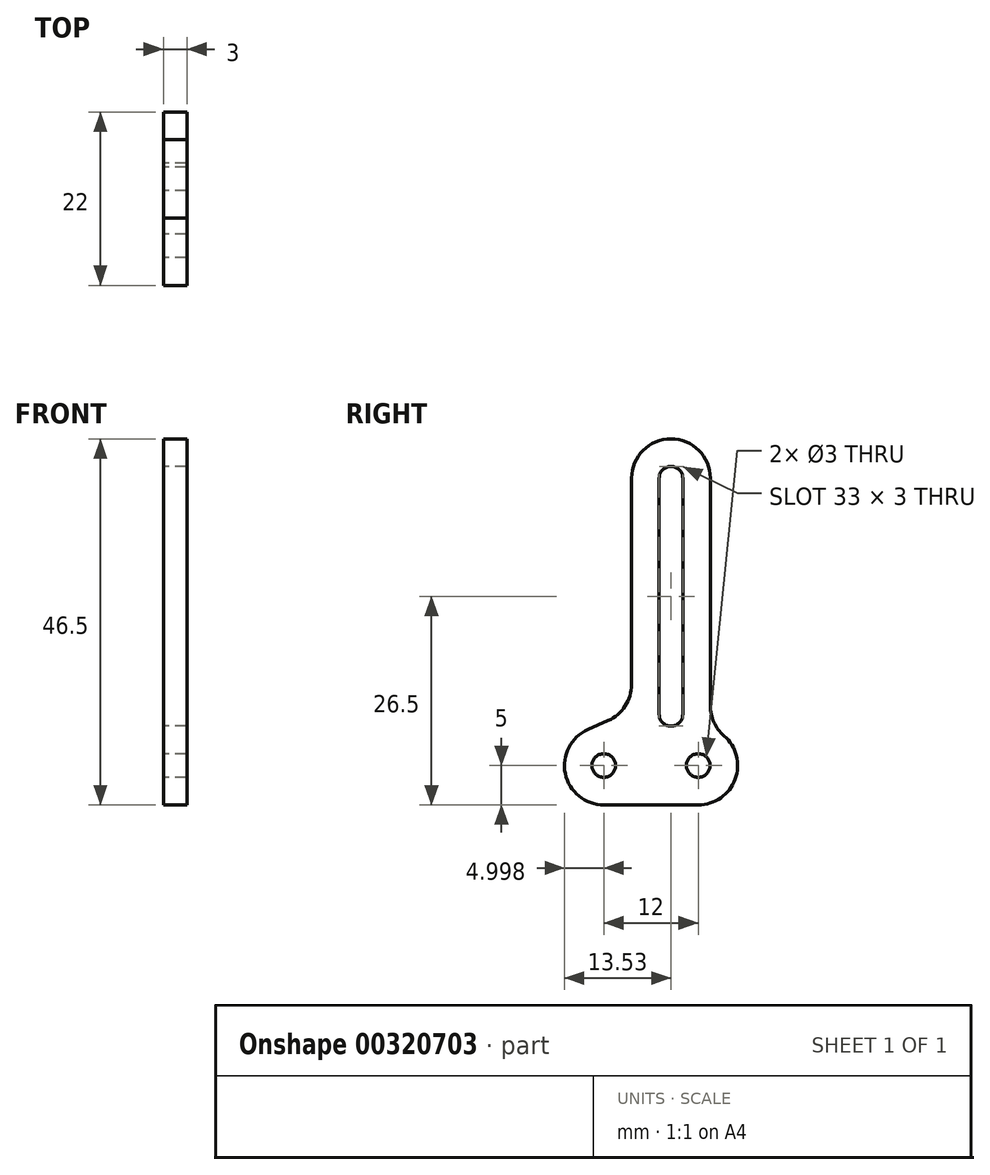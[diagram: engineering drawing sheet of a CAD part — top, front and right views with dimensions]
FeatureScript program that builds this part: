
annotation { "Feature Type Name" : "Feature", "Feature Type Description" : "" }
export const myFeature = defineFeature(function(context is Context, id is Id, definition is map)
    precondition{}
    {
        {
            var Q0;
            Q0=qCreatedBy(makeId("Right.planeOp"),FACE);
            var sketch = newSketch(context, id + "F0", { "sketchPlane" : qUnion([Q0])});
            skCircle(sketch, "E0", {"center": v(-8.53, 0) * mm, "radius": 1.5 * mm});
            skCircle(sketch, "E1", {"center": v(3.47, 0) * mm, "radius": 1.5 * mm});
            skArc(sketch, "E2", {"start": v(5, 36.5) * mm, "mid": v(0, 41.5) * mm, "end": v(-5, 36.5) * mm});
            skArc(sketch, "E3", {"start": v(3.47, -5) * mm, "mid": v(8.15, -1.74) * mm, "end": v(6.73, 3.79) * mm});
            skArc(sketch, "E4", {"start": v(-8.53, -5) * mm, "mid": v(-13.42, -1.03) * mm, "end": v(-10.55, 4.57) * mm});
            skLineSegment(sketch, "E5", {"start": v(-8.53, -5) * mm, "end": v(3.47, -5) * mm});
            skLineSegment(sketch, "E6", {"start": v(-5, 36.5) * mm, "end": v(-5, 10.28) * mm});
            skLineSegment(sketch, "E7", {"start": v(5, 36.5) * mm, "end": v(5, 7.57) * mm});
            skArc(sketch, "E8", {"start": v(5, 7.57) * mm, "mid": v(5.45, 5.49) * mm, "end": v(6.73, 3.79) * mm});
            skArc(sketch, "E9", {"start": v(1.5, 36.5) * mm, "mid": v(0, 38) * mm, "end": v(-1.5, 36.5) * mm});
            skArc(sketch, "E10", {"start": v(-1.5, 6.5) * mm, "mid": v(0, 5) * mm, "end": v(1.5, 6.5) * mm});
            skLineSegment(sketch, "E11", {"start": v(-1.5, 36.5) * mm, "end": v(-1.5, 6.5) * mm});
            skLineSegment(sketch, "E12", {"start": v(1.5, 6.5) * mm, "end": v(1.5, 36.5) * mm});
            skLineSegment(sketch, "E13", {"start": v(-10.55, 4.57) * mm, "end": v(-7.98, 5.7) * mm});
            skArc(sketch, "E14", {"start": v(-7.98, 5.7) * mm, "mid": v(-5.81, 7.55) * mm, "end": v(-5, 10.28) * mm});
            skSolve(sketch);
        }
        {
            var Q0;
            Q0=makeQuery(id+"F0.imprint","IMPRINT",FACE,{"disambiguationData":[TD([[makeQuery(id+"F0.imprint","IMPRINT",EDGE,{"derivedFrom":sQuery(id+"F0.wireOp",EDGE,"E0")}),-1.0]])]});
            extrude(context, id + "F1", {"entities" : qUnion([Q0]), "depth" : 3 * mm});
        }
    });
